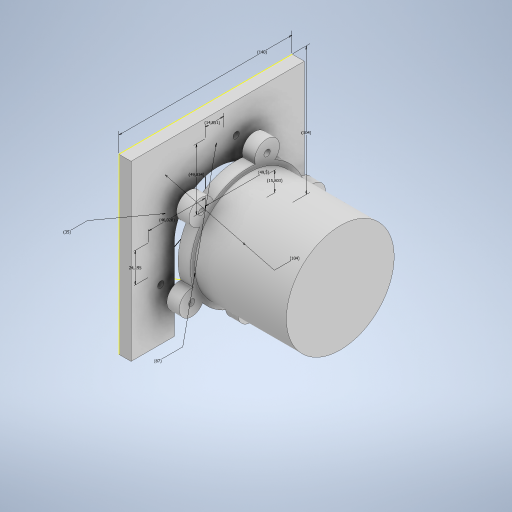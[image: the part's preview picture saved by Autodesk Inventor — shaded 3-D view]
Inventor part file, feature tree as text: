
AUTODESK INVENTOR PART (.ipt)
format: ipt  version: 2023 (Build 270158000, 158)  size: 407,552 bytes
history: native  units: mm
features: sketch x6, extrude x5, other x1, projected_geometry x1
ambient origin geometry x8: Origin, YZ Plane, XZ Plane, XY Plane, X Axis, Y Axis, Z Axis, Center Point
bodies: Body1 (feature_tree)
feature tree (13):
  other  "Твердое тело1"
  extrude  "Выдавливание1"  Depth=10.0mm TaperAngle=0.0deg
  extrude  "Выдавливание2"  Depth=87.0mm
  extrude  "Выдавливание3"  Depth=74.0mm TaperAngle=0.0deg
  extrude  "Выдавливание4"  Depth=70.0mm
  extrude  "Выдавливание5"  Depth=5.0mm TaperAngle=0.0deg
  sketch  "Эскиз7"
  sketch  "Эскиз1"
  sketch  "Эскиз2"
  sketch  "Эскиз3"
  sketch  "Эскиз4"
  sketch  "Эскиз6"
  projected_geometry  "Спроецированная петля1"
